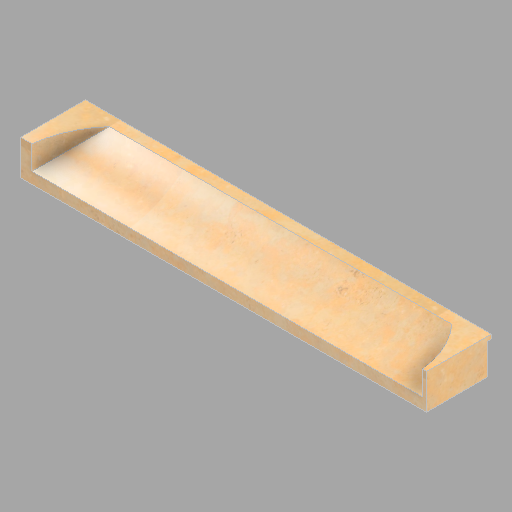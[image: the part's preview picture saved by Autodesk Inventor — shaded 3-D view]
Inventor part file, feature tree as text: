
AUTODESK INVENTOR PART (.ipt)
format: ipt  version: 2022.2 (Build 262287010, 287A)  size: 228,352 bytes
history: native  units: in
note: dims shown in document units (in); Inventor stores cm internally (conversion verified against a paired STEP export)
features: other x1, direct_edit x1, revolve x1
ambient origin geometry x8: Origin, YZ Plane, XZ Plane, XY Plane, X Axis, Y Axis, Z Axis, Center Point
bodies: Solid1 (feature_tree)
feature tree (3):
  other  "North (4) (2)"
  direct_edit  "Direct Edit1"
  revolve  "Rotate1"  Angle=90.0deg
